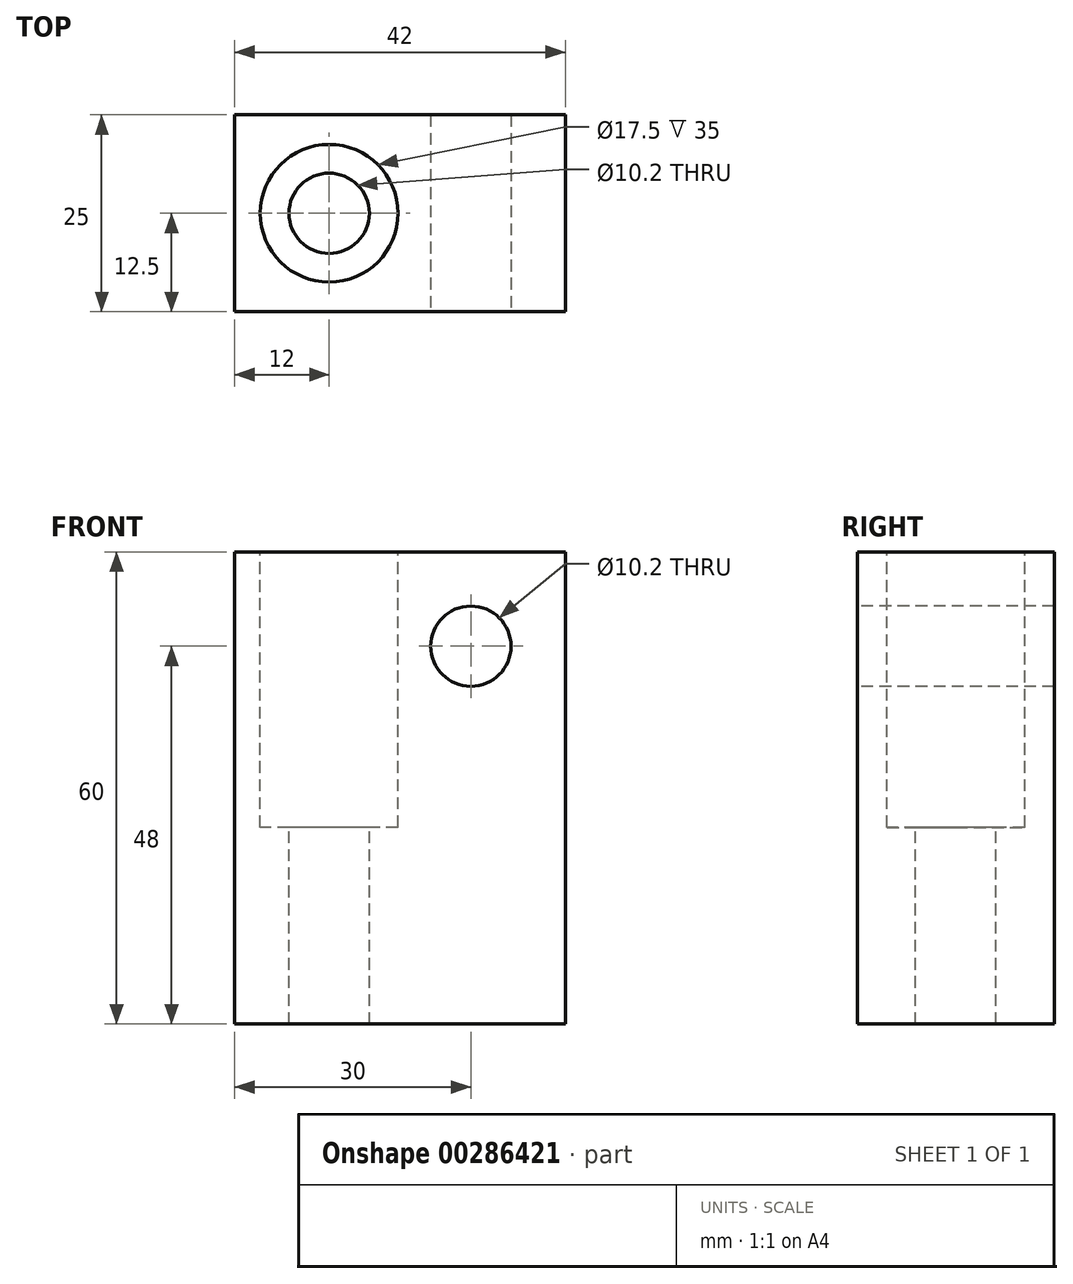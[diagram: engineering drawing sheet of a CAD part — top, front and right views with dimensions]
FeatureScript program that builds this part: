
annotation { "Feature Type Name" : "Feature", "Feature Type Description" : "" }
export const myFeature = defineFeature(function(context is Context, id is Id, definition is map)
    precondition{}
    {
        {
            var Q0;
            Q0=qCreatedBy(makeId("Top.planeOp"),FACE);
            var sketch = newSketch(context, id + "F0", { "sketchPlane" : qUnion([Q0])});
            skLineSegment(sketch, "E0", {"start": v(0, 0) * mm, "end": v(42, 0) * mm});
            skLineSegment(sketch, "E1", {"start": v(42, 0) * mm, "end": v(42, 25) * mm});
            skLineSegment(sketch, "E2", {"start": v(42, 25) * mm, "end": v(0, 25) * mm});
            skLineSegment(sketch, "E3", {"start": v(0, 25) * mm, "end": v(0, 0) * mm});
            skSolve(sketch);
        }
        {
            var Q0;
            Q0 = qSketchRegion(id + "F0", true);
            extrude(context, id + "F1", {"entities" : qUnion([Q0]), "depth" : 60 * mm});
        }
        {
            var Q0;
            Q0=makeQuery(id+"F1.opExtrude","CAP_FACE",FACE,{"disambiguationData":[OSD([sQuery(id+"F0.wireOp",EDGE,"E0"),sQuery(id+"F0.wireOp",EDGE,"E1"),sQuery(id+"F0.wireOp",EDGE,"E2"),sQuery(id+"F0.wireOp",EDGE,"E3")])],"isStart":false});
            cPlane(context, id + "F2", {"entities" : qUnion([Q0]), "cplaneType" : CPlaneType.OFFSET, "offset" : 0 * mm, "width" : 150 * mm, "height" : 150 * mm});
        }
        {
            var Q0;
            Q0=qCreatedBy(id+"F2.planeOp",FACE);
            var sketch = newSketch(context, id + "F3", { "sketchPlane" : qUnion([Q0])});
            skCircle(sketch, "E4", {"center": v(12, 12.5) * mm, "radius": 8.75 * mm});
            skSolve(sketch);
        }
        {
            var Q0;
            Q0 = qSketchRegion(id + "F3", true);
            extrude(context, id + "F4", {"entities" : qUnion([Q0]), "operationType" : NewBodyOperationType.REMOVE, "oppositeDirection" : true, "depth" : 35 * mm});
        }
        {
            var Q0;
            Q0=makeQuery(id+"F1.opExtrude","CAP_FACE",FACE,{"disambiguationData":[OSD([sQuery(id+"F0.wireOp",EDGE,"E0"),sQuery(id+"F0.wireOp",EDGE,"E1"),sQuery(id+"F0.wireOp",EDGE,"E2"),sQuery(id+"F0.wireOp",EDGE,"E3")])],"isStart":false});
            cPlane(context, id + "F5", {"entities" : qUnion([Q0]), "cplaneType" : CPlaneType.OFFSET, "offset" : 0 * mm, "width" : 150 * mm, "height" : 150 * mm});
        }
        {
            var Q0;
            Q0=qCreatedBy(id+"F5.planeOp",FACE);
            var sketch = newSketch(context, id + "F6", { "sketchPlane" : qUnion([Q0])});
            skCircle(sketch, "E5", {"center": v(12, 12.5) * mm, "radius": 5.1 * mm});
            skSolve(sketch);
        }
        {
            var Q0;
            Q0 = qSketchRegion(id + "F6", true);
            extrude(context, id + "F7", {"entities" : qUnion([Q0]), "operationType" : NewBodyOperationType.REMOVE, "oppositeDirection" : true, "depth" : 100 * mm});
        }
        {
            var Q0;
            Q0=makeQuery(id+"F1.opExtrude","SWEPT_FACE",FACE,{"disambiguationData":[OSD([sQuery(id+"F0.wireOp",EDGE,"E0")])]});
            cPlane(context, id + "F8", {"entities" : qUnion([Q0]), "cplaneType" : CPlaneType.OFFSET, "offset" : 0 * mm, "width" : 150 * mm, "height" : 150 * mm});
        }
        {
            var Q0;
            Q0=qCreatedBy(id+"F8.planeOp",FACE);
            var sketch = newSketch(context, id + "F9", { "sketchPlane" : qUnion([Q0])});
            skCircle(sketch, "E6", {"center": v(30, 48) * mm, "radius": 5.1 * mm});
            skSolve(sketch);
        }
        {
            var Q0;
            Q0 = qSketchRegion(id + "F9", true);
            extrude(context, id + "F10", {"entities" : qUnion([Q0]), "operationType" : NewBodyOperationType.REMOVE, "oppositeDirection" : true, "depth" : 80 * mm});
        }
    });
